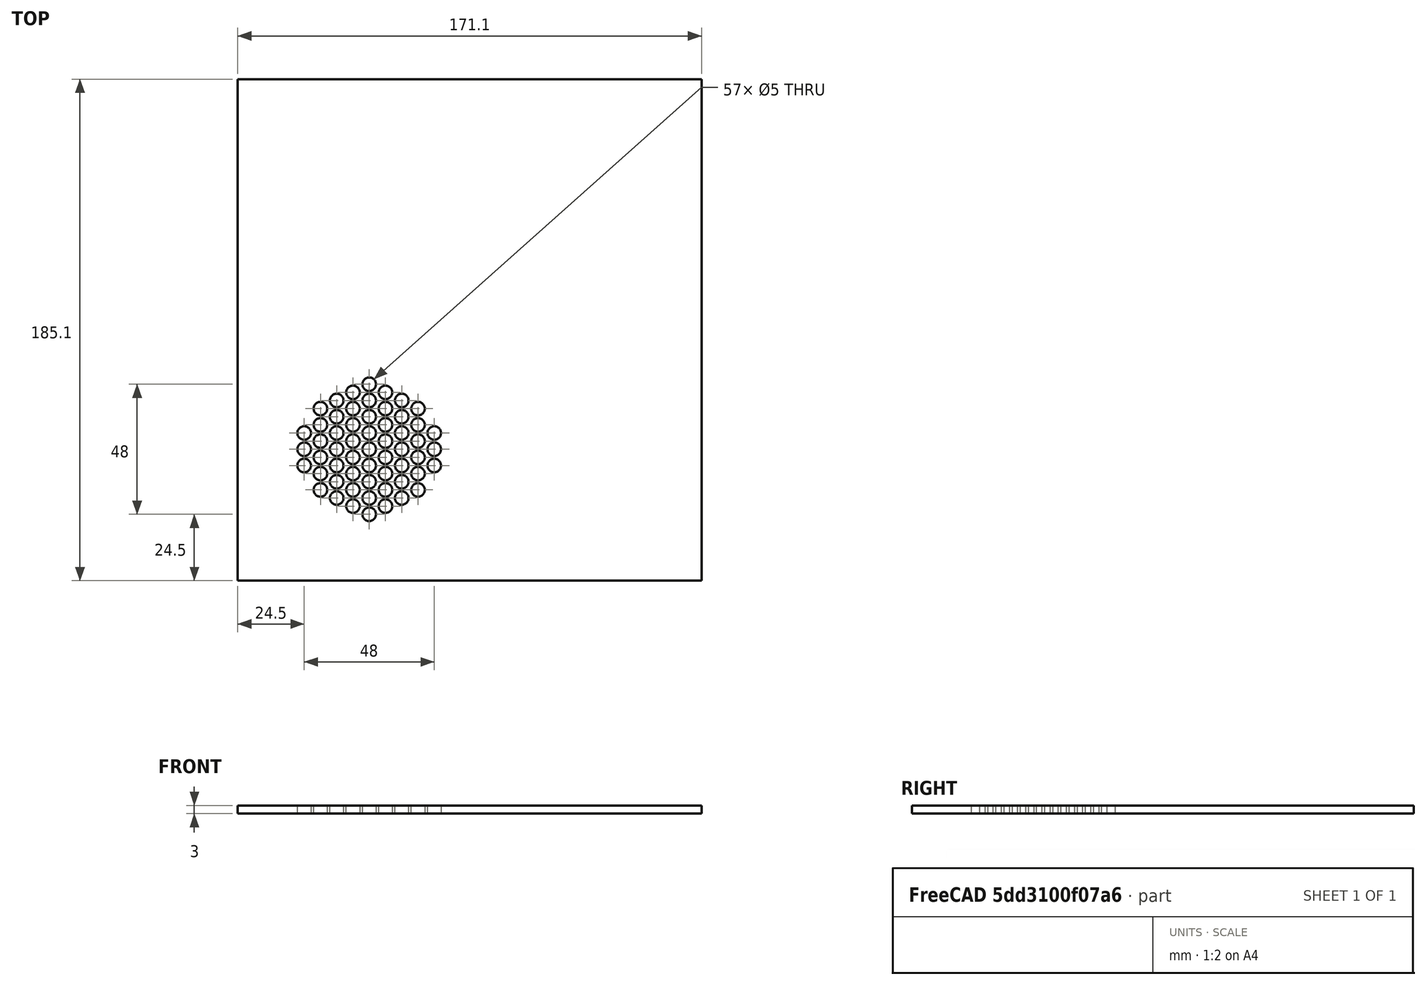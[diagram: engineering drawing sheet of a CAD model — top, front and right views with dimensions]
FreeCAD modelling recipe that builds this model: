
FCSTD DOCUMENT  (FreeCAD 0.21R33771 (Git))
Label: Back_Panel
License: All rights reserved
LicenseURL: http://en.wikipedia.org/wiki/All_rights_reserved
objects: Sketcher::SketchObject×1, PartDesign::Pad×1, PartDesign::CoordinateSystem×1, PartDesign::Body×1
note: 5 computed .brp shape members not serialized (recipe doc carries the construction recipe); baked Part::Feature solids carry a one-line shape summary decoded from their .brp
EXTERNAL_REF file=Noise_Toaster_Classic.FCStd obj=Spreadsheet

FEATURE [Sketcher::SketchObject] Sketch
  FullyConstrained = true
  MapMode = 5
  Support = -> [XY_Plane]
  expr: Constraints[10] = Noise_Toaster_Classic#<<measurements>>.Back_width
  expr: Constraints[9] = Noise_Toaster_Classic#<<measurements>>.Back_height
  sketch-geometry (61):
    g0: LineSegment StartX=0 StartY=0 StartZ=0 EndX=171.1 EndY=0 EndZ=0
    g1: LineSegment StartX=171.1 StartY=0 StartZ=0 EndX=171.1 EndY=185.1 EndZ=0
    g2: LineSegment StartX=171.1 StartY=185.1 StartZ=0 EndX=0 EndY=185.1 EndZ=0
    g3: LineSegment StartX=0 StartY=185.1 StartZ=0 EndX=0 EndY=0 EndZ=0
    g4: Circle CenterX=48.5 CenterY=48.5 CenterZ=0 NormalX=0 NormalY=0 NormalZ=1 AngleXU=0 Radius=2.5
    g5: Circle CenterX=48.5 CenterY=54.5 CenterZ=0 NormalX=0 NormalY=0 NormalZ=1 AngleXU=0 Radius=2.5
    g6: Circle CenterX=48.5 CenterY=60.5 CenterZ=0 NormalX=0 NormalY=0 NormalZ=1 AngleXU=0 Radius=2.5
    g7: Circle CenterX=48.5 CenterY=66.5 CenterZ=0 NormalX=0 NormalY=0 NormalZ=1 AngleXU=0 Radius=2.5
    g8: Circle CenterX=48.5 CenterY=72.5 CenterZ=0 NormalX=0 NormalY=0 NormalZ=1 AngleXU=0 Radius=2.5
    g9: Circle CenterX=48.5 CenterY=42.5 CenterZ=0 NormalX=0 NormalY=0 NormalZ=1 AngleXU=0 Radius=2.5
    g10: Circle CenterX=48.5 CenterY=36.5 CenterZ=0 NormalX=0 NormalY=0 NormalZ=1 AngleXU=0 Radius=2.5
    g11: Circle CenterX=48.5 CenterY=30.5 CenterZ=0 NormalX=0 NormalY=0 NormalZ=1 AngleXU=0 Radius=2.5
    g12: Circle CenterX=48.5 CenterY=24.5 CenterZ=0 NormalX=0 NormalY=0 NormalZ=1 AngleXU=0 Radius=2.5
    g13: Circle CenterX=36.5 CenterY=48.5 CenterZ=0 NormalX=0 NormalY=0 NormalZ=1 AngleXU=0 Radius=2.5
    g14: Circle CenterX=36.5 CenterY=54.5 CenterZ=0 NormalX=0 NormalY=0 NormalZ=1 AngleXU=0 Radius=2.5
    g15: Circle CenterX=36.5 CenterY=60.5 CenterZ=0 NormalX=0 NormalY=0 NormalZ=1 AngleXU=0 Radius=2.5
    g16: Circle CenterX=36.5 CenterY=66.5 CenterZ=0 NormalX=0 NormalY=0 NormalZ=1 AngleXU=0 Radius=2.5
    g17: Circle CenterX=36.5 CenterY=42.5 CenterZ=0 NormalX=0 NormalY=0 NormalZ=1 AngleXU=0 Radius=2.5
    g18: Circle CenterX=36.5 CenterY=36.5 CenterZ=0 NormalX=0 NormalY=0 NormalZ=1 AngleXU=0 Radius=2.5
    g19: Circle CenterX=36.5 CenterY=30.5 CenterZ=0 NormalX=0 NormalY=0 NormalZ=1 AngleXU=0 Radius=2.5
    g20: Circle CenterX=24.5 CenterY=48.5 CenterZ=0 NormalX=0 NormalY=0 NormalZ=1 AngleXU=0 Radius=2.5
    g21: Circle CenterX=24.5 CenterY=54.5 CenterZ=0 NormalX=0 NormalY=0 NormalZ=1 AngleXU=0 Radius=2.5
    g22: Circle CenterX=24.5 CenterY=42.5 CenterZ=0 NormalX=0 NormalY=0 NormalZ=1 AngleXU=0 Radius=2.5
    g23: Circle CenterX=42.5 CenterY=51.5 CenterZ=0 NormalX=0 NormalY=0 NormalZ=1 AngleXU=0 Radius=2.5
    g24: Circle CenterX=42.5 CenterY=45.5 CenterZ=0 NormalX=0 NormalY=0 NormalZ=1 AngleXU=0 Radius=2.5
    g25: Circle CenterX=42.5 CenterY=39.5 CenterZ=0 NormalX=0 NormalY=0 NormalZ=1 AngleXU=0 Radius=2.5
    g26: Circle CenterX=42.5 CenterY=33.5 CenterZ=0 NormalX=0 NormalY=0 NormalZ=1 AngleXU=0 Radius=2.5
    g27: Circle CenterX=42.5 CenterY=27.5 CenterZ=0 NormalX=0 NormalY=0 NormalZ=1 AngleXU=0 Radius=2.5
    g28: Circle CenterX=42.5 CenterY=57.5 CenterZ=0 NormalX=0 NormalY=0 NormalZ=1 AngleXU=0 Radius=2.5
    g29: Circle CenterX=42.5 CenterY=63.5 CenterZ=0 NormalX=0 NormalY=0 NormalZ=1 AngleXU=0 Radius=2.5
    g30: Circle CenterX=42.5 CenterY=69.5 CenterZ=0 NormalX=0 NormalY=0 NormalZ=1 AngleXU=0 Radius=2.5
    g31: Circle CenterX=30.5 CenterY=51.5 CenterZ=0 NormalX=0 NormalY=0 NormalZ=1 AngleXU=0 Radius=2.5
    g32: Circle CenterX=30.5 CenterY=57.5 CenterZ=0 NormalX=0 NormalY=0 NormalZ=1 AngleXU=0 Radius=2.5
    g33: Circle CenterX=30.5 CenterY=63.5 CenterZ=0 NormalX=0 NormalY=0 NormalZ=1 AngleXU=0 Radius=2.5
    g34: Circle CenterX=30.5 CenterY=45.5 CenterZ=0 NormalX=0 NormalY=0 NormalZ=1 AngleXU=0 Radius=2.5
    g35: Circle CenterX=30.5 CenterY=39.5 CenterZ=0 NormalX=0 NormalY=0 NormalZ=1 AngleXU=0 Radius=2.5
    g36: Circle CenterX=30.5 CenterY=33.5 CenterZ=0 NormalX=0 NormalY=0 NormalZ=1 AngleXU=0 Radius=2.5
    g37: Circle CenterX=54.5 CenterY=69.5 CenterZ=0 NormalX=0 NormalY=0 NormalZ=1 AngleXU=0 Radius=2.5
    g38: Circle CenterX=54.5 CenterY=63.5 CenterZ=0 NormalX=0 NormalY=0 NormalZ=1 AngleXU=0 Radius=2.5
    g39: Circle CenterX=54.5 CenterY=57.5 CenterZ=0 NormalX=0 NormalY=0 NormalZ=1 AngleXU=0 Radius=2.5
    g40: Circle CenterX=54.5 CenterY=51.5 CenterZ=0 NormalX=0 NormalY=0 NormalZ=1 AngleXU=0 Radius=2.5
    g41: Circle CenterX=54.5 CenterY=45.5 CenterZ=0 NormalX=0 NormalY=0 NormalZ=1 AngleXU=0 Radius=2.5
    g42: Circle CenterX=54.5 CenterY=39.5 CenterZ=0 NormalX=0 NormalY=0 NormalZ=1 AngleXU=0 Radius=2.5
    g43: Circle CenterX=54.5 CenterY=33.5 CenterZ=0 NormalX=0 NormalY=0 NormalZ=1 AngleXU=0 Radius=2.5
    g44: Circle CenterX=54.5 CenterY=27.5 CenterZ=0 NormalX=0 NormalY=0 NormalZ=1 AngleXU=0 Radius=2.5
    g45: Circle CenterX=60.5 CenterY=66.5 CenterZ=0 NormalX=0 NormalY=0 NormalZ=1 AngleXU=0 Radius=2.5
    g46: Circle CenterX=60.5 CenterY=60.5 CenterZ=0 NormalX=0 NormalY=0 NormalZ=1 AngleXU=0 Radius=2.5
    g47: Circle CenterX=60.5 CenterY=54.5 CenterZ=0 NormalX=0 NormalY=0 NormalZ=1 AngleXU=0 Radius=2.5
    g48: Circle CenterX=60.5 CenterY=48.5 CenterZ=0 NormalX=0 NormalY=0 NormalZ=1 AngleXU=0 Radius=2.5
    g49: Circle CenterX=60.5 CenterY=42.5 CenterZ=0 NormalX=0 NormalY=0 NormalZ=1 AngleXU=0 Radius=2.5
    g50: Circle CenterX=60.5 CenterY=36.5 CenterZ=0 NormalX=0 NormalY=0 NormalZ=1 AngleXU=0 Radius=2.5
    g51: Circle CenterX=60.5 CenterY=30.5 CenterZ=0 NormalX=0 NormalY=0 NormalZ=1 AngleXU=0 Radius=2.5
    g52: Circle CenterX=66.5 CenterY=63.5 CenterZ=0 NormalX=0 NormalY=0 NormalZ=1 AngleXU=0 Radius=2.5
    g53: Circle CenterX=66.5 CenterY=57.5 CenterZ=0 NormalX=0 NormalY=0 NormalZ=1 AngleXU=0 Radius=2.5
    g54: Circle CenterX=66.5 CenterY=51.5 CenterZ=0 NormalX=0 NormalY=0 NormalZ=1 AngleXU=0 Radius=2.5
    g55: Circle CenterX=66.5 CenterY=45.5 CenterZ=0 NormalX=0 NormalY=0 NormalZ=1 AngleXU=0 Radius=2.5
    g56: Circle CenterX=66.5 CenterY=39.5 CenterZ=0 NormalX=0 NormalY=0 NormalZ=1 AngleXU=0 Radius=2.5
    g57: Circle CenterX=66.5 CenterY=33.5 CenterZ=0 NormalX=0 NormalY=0 NormalZ=1 AngleXU=0 Radius=2.5
    g58: Circle CenterX=72.5 CenterY=54.5 CenterZ=0 NormalX=0 NormalY=0 NormalZ=1 AngleXU=0 Radius=2.5
    g59: Circle CenterX=72.5 CenterY=48.5 CenterZ=0 NormalX=0 NormalY=0 NormalZ=1 AngleXU=0 Radius=2.5
    g60: Circle CenterX=72.5 CenterY=42.5 CenterZ=0 NormalX=0 NormalY=0 NormalZ=1 AngleXU=0 Radius=2.5
  constraints (182):
    c: Coincident(g0,g1)
    c: Coincident(g1,g2)
    c: Coincident(g2,g3)
    c: Coincident(g3,g0)
    c: Horizontal(g0)
    c: Horizontal(g2)
    c: Vertical(g1)
    c: Vertical(g3)
    c: Coincident(g0,g-1)
    c: DistanceX(g2,g2) = 171.1
    c: DistanceY(g3,g3) = 185.1
    c: Radius(g4) = 2.5
    c: Vertical(g7,g6)
    c: Vertical(g6,g5)
    c: Equal(g4,g5)
    c: Equal(g5,g6)
    c: Equal(g6,g7)
    c: Vertical(g8,g7)
    c: Equal(g8,g7)
    c: Distance(g6,g5) = 6
    c: Distance(g7,g6) = 6
    c: Distance(g8,g7) = 6
    c: Equal(g9,g10)
    c: Equal(g10,g11)
    c: Equal(g11,g12)
    c: Equal(g4,g9)
    c: Vertical(g9,g10)
    c: Vertical(g10,g11)
    c: Vertical(g11,g12)
    c: Distance(g9,g10) = 6
    c: Distance(g10,g11) = 6
    c: Distance(g11,g12) = 6
    c: Vertical(g13,g14)
    c: Vertical(g14,g15)
    c: Vertical(g15,g16)
    c: Radius(g13) = 2.5
    c: Equal(g13,g14)
    c: Equal(g14,g15)
    c: Equal(g15,g16)
    c: Equal(g13,g17)
    c: Equal(g17,g18)
    c: Equal(g18,g19)
    c: Vertical(g13,g17)
    c: Vertical(g17,g18)
    c: Vertical(g18,g19)
    c: Distance(g16,g15) = 6
    c: Distance(g15,g14) = 6
    c: Distance(g13,g14) = 6
    c: Distance(g13,g17) = 6
    c: Distance(g18,g17) = 6
    c: Distance(g19,g18) = 6
    c: Vertical(g22,g20)
    c: Vertical(g20,g21)
    c: Distance(g13,g20) = 12
    c: Radius(g20) = 2.5
    c: Equal(g20,g21)
    c: Distance(g20,g21) = 6
    c: Distance(g20,g22) = 6
    c: Horizontal(g13,g20)
    c: Equal(g20,g22)
    c: Vertical(g34,g35)
    c: Vertical(g35,g36)
    c: Vertical(g36,g31)
    c: Vertical(g31,g32)
    c: Vertical(g32,g33)
    c: Vertical(g26,g27)
    c: Vertical(g27,g25)
    c: Vertical(g25,g24)
    c: Vertical(g24,g23)
    c: Vertical(g23,g28)
    c: Vertical(g28,g29)
    c: Vertical(g29,g30)
    c: Equal(g4,g24)
    c: Equal(g24,g25)
    c: Equal(g25,g26)
    c: Equal(g26,g27)
    c: Equal(g27,g23)
    c: Equal(g23,g28)
    c: Equal(g28,g29)
    c: Equal(g29,g30)
    c: Equal(g30,g33)
    c: Equal(g33,g32)
    c: Equal(g32,g31)
    c: Equal(g31,g34)
    c: Equal(g34,g35)
    c: Equal(g35,g36)
    c: Distance(g30,g29) = 6
    c: Distance(g29,g28) = 6
    c: Distance(g28,g23) = 6
    c: Distance(g23,g24) = 6
    c: Distance(g24,g25) = 6
    c: Distance(g25,g26) = 6
    c: Distance(g26,g27) = 6
    c: Distance(g36,g35) = 6
    c: Distance(g34,g35) = 6
    c: Distance(g31,g34) = 6
    c: Distance(g32,g31) = 6
    c: Distance(g33,g32) = 6
    c: Distance(g23,g31) = 12
    c: Horizontal(g23,g31)
    c: Equal(g11,g43)
    c: Equal(g43,g42)
    c: Equal(g42,g41)
    c: Equal(g41,g40)
    c: Equal(g40,g39)
    c: Equal(g39,g38)
    c: Equal(g38,g37)
    c: Equal(g37,g44)
    c: Vertical(g37,g38)
    c: Vertical(g38,g39)
    c: Vertical(g39,g40)
    c: Vertical(g40,g41)
    c: Vertical(g41,g42)
    c: Vertical(g42,g43)
    c: Vertical(g43,g44)
    c: Horizontal(g37,g30)
    c: DistanceX(g30,g37) = 12
    c: Distance(g37,g38) = 6
    c: Distance(g38,g39) = 6
    c: Distance(g39,g40) = 6
    c: Distance(g40,g41) = 6
    c: Distance(g41,g42) = 6
    c: Distance(g42,g43) = 6
    c: Distance(g43,g44) = 6
    c: Vertical(g45,g46)
    c: Vertical(g46,g47)
    c: Vertical(g47,g48)
    c: Vertical(g48,g49)
    c: Vertical(g49,g50)
    c: Vertical(g50,g51)
    c: Equal(g45,g46)
    c: Equal(g46,g47)
    c: Equal(g47,g48)
    c: Equal(g48,g49)
    c: Equal(g49,g50)
    c: Equal(g50,g51)
    c: Equal(g51,g37)
    c: Horizontal(g45,g7)
    c: Distance(g45,g46) = 6
    c: Distance(g46,g47) = 6
    c: Distance(g47,g48) = 6
    c: Distance(g48,g49) = 6
    c: Distance(g49,g50) = 6
    c: Distance(g50,g51) = 6
    c: Vertical(g52,g53)
    c: Vertical(g53,g54)
    c: Vertical(g54,g55)
    c: Vertical(g55,g56)
    c: Vertical(g56,g57)
    c: Equal(g52,g53)
    c: Equal(g53,g54)
    c: Equal(g54,g55)
    c: Equal(g55,g56)
    c: Equal(g56,g57)
    c: Equal(g57,g45)
    c: DistanceY(g53,g52) = 6
    c: DistanceY(g54,g53) = 6
    c: DistanceY(g55,g54) = 6
    c: DistanceY(g56,g55) = 6
    c: DistanceX(g43,g57) = 12
    c: Horizontal(g57,g43)
    c: Distance(g57,g56) = 6
    c: Equal(g58,g59)
    c: Equal(g59,g60)
    c: Equal(g60,g53)
    c: Vertical(g58,g59)
    c: Vertical(g59,g60)
    c: Horizontal(g59,g48)
    c: DistanceY(g59,g58) = 6
    c: DistanceY(g60,g59) = 6
    c: DistanceX(g48,g59) = 12
    c: Distance(g4,g0) = 48.5
    c: Distance(g4,g3) = 48.5
    c: DistanceX(g4,g40) = 6
    c: DistanceX(g14,g5) = 12
    c: DistanceY(g24,g4) = 3
    c: Vertical(g9,g4)
    c: DistanceY(g9,g4) = 6
    c: DistanceY(g4,g5) = 6
    c: Vertical(g5,g4)
    c: DistanceX(g5,g47) = 12
    c: Horizontal(g5,g14)
FEATURE [PartDesign::Pad] Pad
  Direction = (0,0,1)
  Length = 3
  Length2 = 10
  Profile = -> Sketch
  ReferenceAxis = -> Sketch [N_Axis]
  Reversed = true
  Type = 0
  expr: Length = Noise_Toaster_Classic#<<measurements>>.Back_thickness
FEATURE [PartDesign::CoordinateSystem] BP_LCS
  AttacherType = Attacher::AttachEngine3D
  Support = -> [Pad]
FEATURE [PartDesign::Body] Body  label="Körper"
  Group = -> [Sketch,Pad,BP_LCS]
  Origin = -> Origin
  Tip = -> Pad
